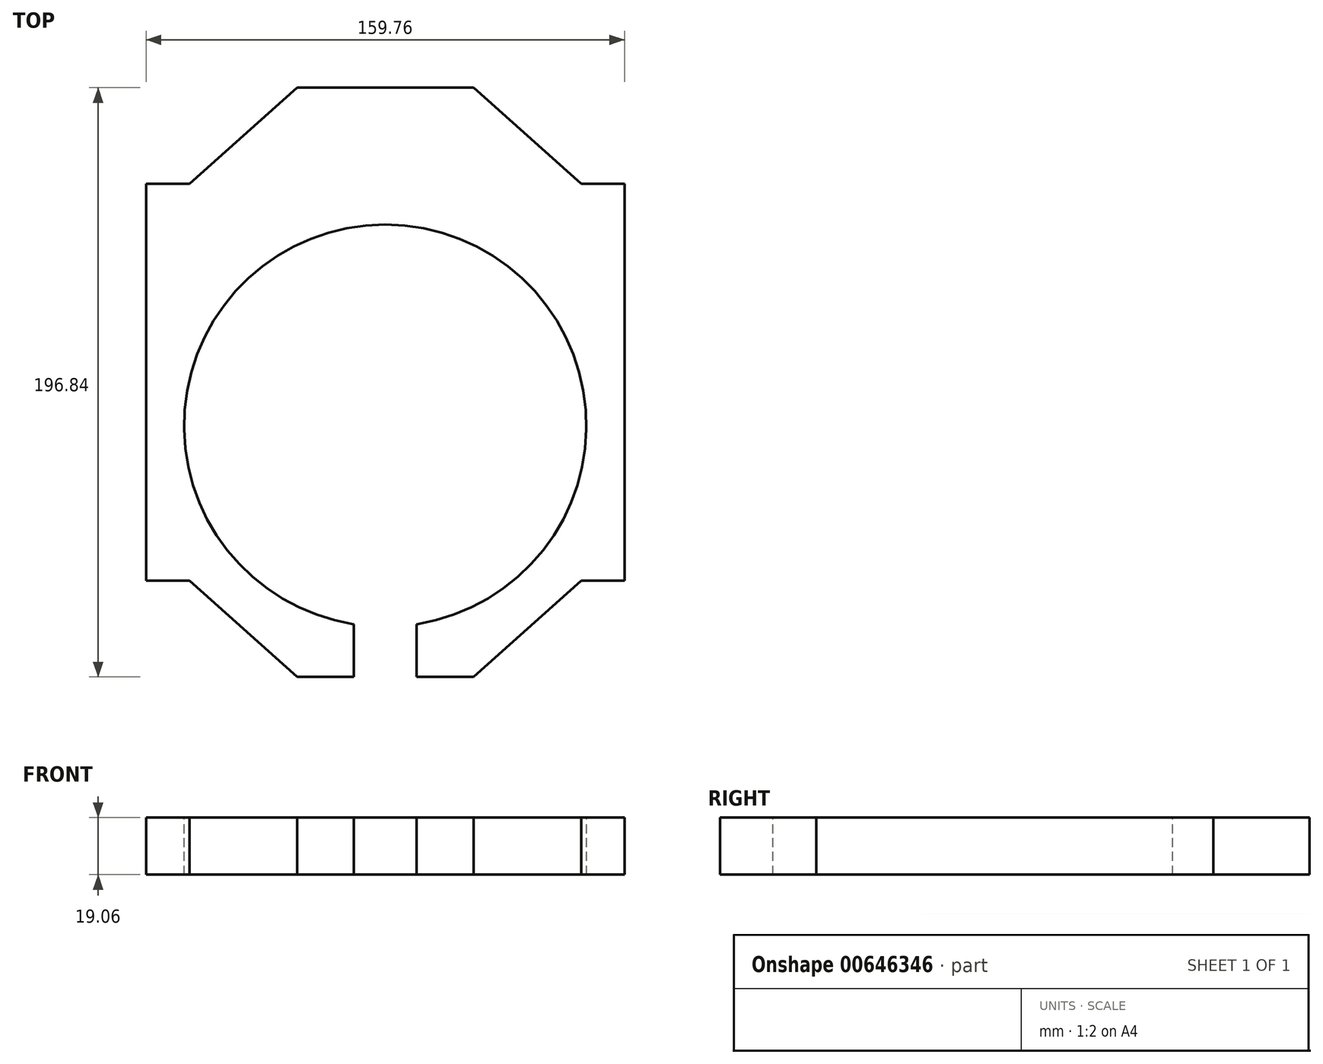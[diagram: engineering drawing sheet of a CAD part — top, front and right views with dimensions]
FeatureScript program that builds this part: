
annotation { "Feature Type Name" : "Feature", "Feature Type Description" : "" }
export const myFeature = defineFeature(function(context is Context, id is Id, definition is map)
    precondition{}
    {
        {
            var Q0;
            Q0=qCreatedBy(makeId("Top.planeOp"),FACE);
            var sketch = newSketch(context, id + "F0", { "sketchPlane" : qUnion([Q0])});
            skLineSegment(sketch, "E0.bottom", {"start": v(29.46, 98.42) * mm, "end": v(-29.46, 98.42) * mm});
            skLineSegment(sketch, "E0.top", {"start": v(29.46, -98.42) * mm, "end": v(-29.46, -98.42) * mm});
            skLineSegment(sketch, "E0.left", {"start": v(29.46, 98.42) * mm, "end": v(29.46, -98.42) * mm});
            skLineSegment(sketch, "E0.right", {"start": v(-29.46, 98.42) * mm, "end": v(-29.46, -98.42) * mm});
            skPoint(sketch, "E0.middle", {"position": v(0, 0) * mm});
            skLineSegment(sketch, "E1.bottom", {"start": v(-65.4, 66.3) * mm, "end": v(65.4, 66.3) * mm});
            skLineSegment(sketch, "E1.top", {"start": v(-65.4, -66.3) * mm, "end": v(65.4, -66.3) * mm});
            skLineSegment(sketch, "E1.left", {"start": v(-65.4, 66.3) * mm, "end": v(-65.4, -66.3) * mm});
            skLineSegment(sketch, "E1.right", {"start": v(65.4, 66.3) * mm, "end": v(65.4, -66.3) * mm});
            skLineSegment(sketch, "E2", {"start": v(-29.46, -98.42) * mm, "end": v(-65.4, -66.3) * mm});
            skLineSegment(sketch, "E3", {"start": v(29.46, -98.42) * mm, "end": v(65.4, -66.3) * mm});
            skLineSegment(sketch, "E4", {"start": v(65.4, 66.3) * mm, "end": v(29.46, 98.42) * mm});
            skLineSegment(sketch, "E5", {"start": v(-65.4, 66.3) * mm, "end": v(-29.46, 98.42) * mm});
            skLineSegment(sketch, "E6.bottom", {"start": v(-79.88, 66.3) * mm, "end": v(79.88, 66.3) * mm});
            skLineSegment(sketch, "E6.top", {"start": v(-79.88, -66.3) * mm, "end": v(79.88, -66.3) * mm});
            skLineSegment(sketch, "E6.left", {"start": v(-79.88, 66.3) * mm, "end": v(-79.88, -66.3) * mm});
            skLineSegment(sketch, "E6.right", {"start": v(79.88, 66.3) * mm, "end": v(79.88, -66.3) * mm});
            skSolve(sketch);
        }
        {
            var Q0;
            Q0=qCreatedBy(makeId("Top.planeOp"),FACE);
            var sketch = newSketch(context, id + "F1", { "sketchPlane" : qUnion([Q0])});
            skSolve(sketch);
        }
        {
            var Q0;
            {var subQ0=sQuery(id+"F0.wireOp",EDGE,"E0.bottom");Q0=makeQuery(id+"F0.imprint","IMPRINT",FACE,{"disambiguationData":[TD([[makeQuery(id+"F0.imprint","IMPRINT",EDGE,{"derivedFrom":subQ0}),1.0]])]});}
            var Q1;
            {var subQ5=sQuery(id+"F0.wireOp",EDGE,"E1.left");Q1=makeQuery(id+"F0.imprint","IMPRINT",FACE,{"disambiguationData":[TD([[makeQuery(id+"F0.imprint","IMPRINT",EDGE,{"derivedFrom":subQ5}),1.0]])]});}
            var Q2;
            {var subQ0=sQuery(id+"F0.wireOp",EDGE,"E5");Q2=makeQuery(id+"F0.imprint","IMPRINT",FACE,{"disambiguationData":[TD([[makeQuery(id+"F0.imprint","IMPRINT",EDGE,{"derivedFrom":subQ0}),-1.0]])]});}
            var Q3;
            {var subQ0=sQuery(id+"F0.wireOp",EDGE,"E1.bottom");var subQ1=sQuery(id+"F0.wireOp",EDGE,"E0.left");var subQ2=makeQuery(id+"F0.imprint","INTERSECT",VERTEX,{"derivedFrom":[subQ1,subQ0]});Q3=makeQuery(id+"F0.imprint","IMPRINT",FACE,{"disambiguationData":[TD([[makeQuery(id+"F0.imprint","IMPRINT",EDGE,{"disambiguationData":[TD([[subQ2,-1.0]])],"derivedFrom":subQ1}),-1.0]])]});}
            var Q4;
            {var subQ5=sQuery(id+"F0.wireOp",EDGE,"E1.right");Q4=makeQuery(id+"F0.imprint","IMPRINT",FACE,{"disambiguationData":[TD([[makeQuery(id+"F0.imprint","IMPRINT",EDGE,{"derivedFrom":subQ5}),-1.0]])]});}
            var Q5;
            {var subQ0=sQuery(id+"F0.wireOp",EDGE,"E4");Q5=makeQuery(id+"F0.imprint","IMPRINT",FACE,{"disambiguationData":[TD([[makeQuery(id+"F0.imprint","IMPRINT",EDGE,{"derivedFrom":subQ0}),1.0]])]});}
            var Q6;
            {var subQ0=sQuery(id+"F0.wireOp",EDGE,"E3");Q6=makeQuery(id+"F0.imprint","IMPRINT",FACE,{"disambiguationData":[TD([[makeQuery(id+"F0.imprint","IMPRINT",EDGE,{"derivedFrom":subQ0}),1.0]])]});}
            var Q7;
            {var subQ0=sQuery(id+"F0.wireOp",EDGE,"E0.top");Q7=makeQuery(id+"F0.imprint","IMPRINT",FACE,{"disambiguationData":[TD([[makeQuery(id+"F0.imprint","IMPRINT",EDGE,{"derivedFrom":subQ0}),-1.0]])]});}
            var Q8;
            {var subQ0=sQuery(id+"F0.wireOp",EDGE,"E2");Q8=makeQuery(id+"F0.imprint","IMPRINT",FACE,{"disambiguationData":[TD([[makeQuery(id+"F0.imprint","IMPRINT",EDGE,{"derivedFrom":subQ0}),-1.0]])]});}
            var Q9;
            Q9=qSketchRegion(id+"F1",true);
            var Q10;
            {var subQ0=sQuery(id+"F0.wireOp",EDGE,"E1.left");Q10=makeQuery(id+"F0.imprint","IMPRINT",FACE,{"disambiguationData":[TD([[makeQuery(id+"F0.imprint","IMPRINT",EDGE,{"derivedFrom":subQ0}),-1.0]])]});}
            var Q11;
            {var subQ0=sQuery(id+"F0.wireOp",EDGE,"E1.right");Q11=makeQuery(id+"F0.imprint","IMPRINT",FACE,{"disambiguationData":[TD([[makeQuery(id+"F0.imprint","IMPRINT",EDGE,{"derivedFrom":subQ0}),1.0]])]});}
            extrude(context, id + "F2", {"entities" : qUnion([Q0, Q1, Q2, Q3, Q4, Q5, Q6, Q7, Q8, Q9, Q10, Q11]), "endBound" : BoundingType.SYMMETRIC, "depth" : 19.05 * mm, "offsetDistance" : 25.4 * mm});
        }
        {
            var Q0;
            Q0=qCreatedBy(makeId("Top.planeOp"),FACE);
            var sketch = newSketch(context, id + "F3", { "sketchPlane" : qUnion([Q0])});
            skLineSegment(sketch, "E7", {"start": v(-10.48, -98.42) * mm, "end": v(10.48, -98.42) * mm});
            skLineSegment(sketch, "E8", {"start": v(-10.48, -98.42) * mm, "end": v(-10.48, -1.9) * mm});
            skLineSegment(sketch, "E9", {"start": v(-10.48, -1.9) * mm, "end": v(10.48, -1.9) * mm});
            skLineSegment(sketch, "E10", {"start": v(10.48, -1.9) * mm, "end": v(10.48, -98.42) * mm});
            skSolve(sketch);
        }
        {
            var Q0;
            Q0=qSketchRegion(id+"F3",true);
            extrude(context, id + "F4", {"entities" : qUnion([Q0]), "operationType" : NewBodyOperationType.REMOVE, "endBound" : BoundingType.SYMMETRIC, "oppositeDirection" : true, "depth" : 19.05 * mm, "offsetDistance" : 25.4 * mm});
        }
        {
            var Q0;
            Q0=qCreatedBy(makeId("Top.planeOp"),FACE);
            var sketch = newSketch(context, id + "F5", { "sketchPlane" : qUnion([Q0])});
            skCircle(sketch, "E11", {"center": v(0, -14.48) * mm, "radius": 67.18 * mm});
            skSolve(sketch);
        }
        {
            var Q0;
            Q0 = qSketchRegion(id + "F5", true);
            extrude(context, id + "F6", {"entities" : qUnion([Q0]), "operationType" : NewBodyOperationType.REMOVE, "endBound" : BoundingType.SYMMETRIC, "oppositeDirection" : true, "depth" : 19.05 * mm, "offsetDistance" : 25.4 * mm});
        }
    });
